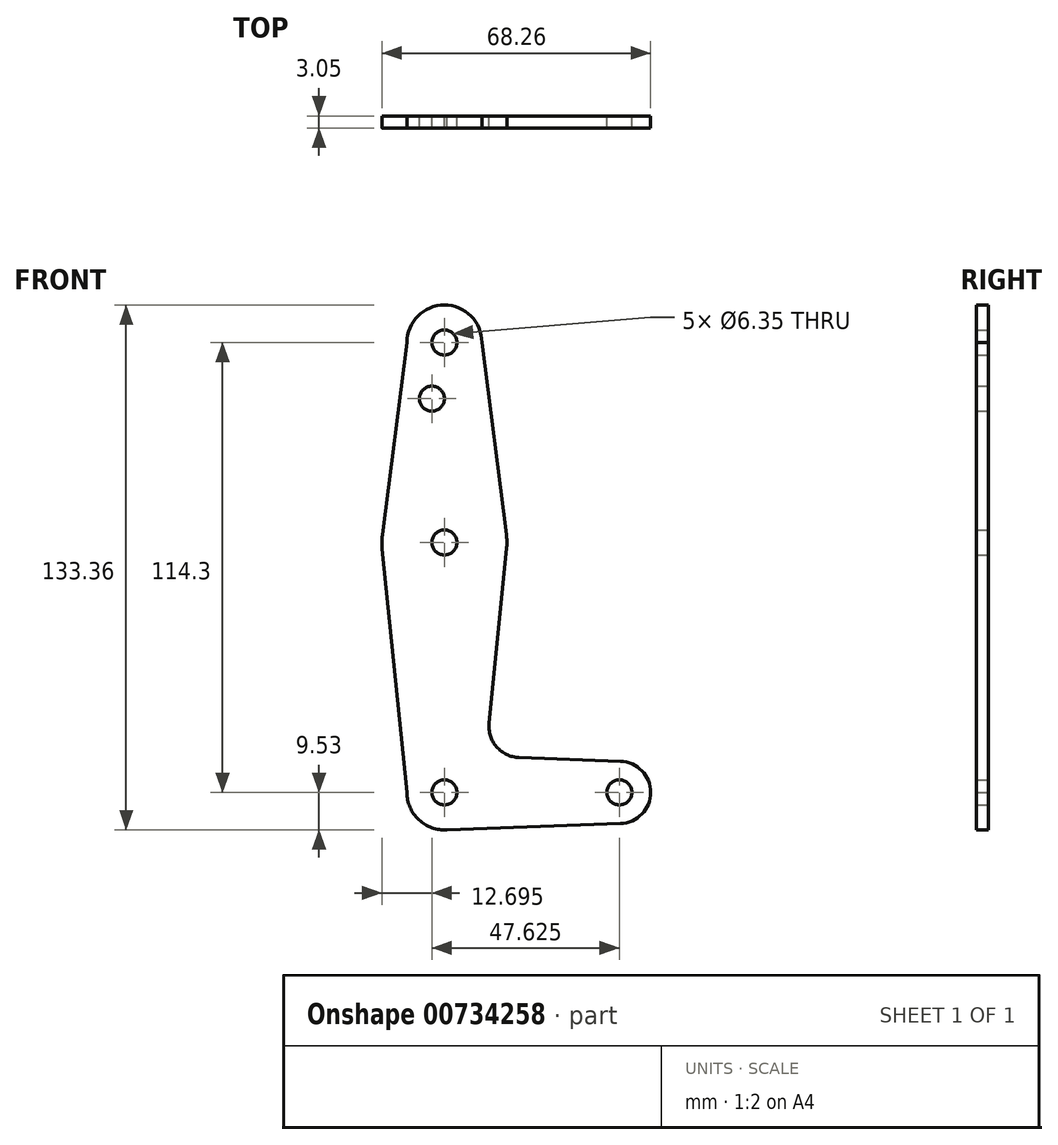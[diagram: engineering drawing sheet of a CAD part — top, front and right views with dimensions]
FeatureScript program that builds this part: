
annotation { "Feature Type Name" : "Feature", "Feature Type Description" : "" }
export const myFeature = defineFeature(function(context is Context, id is Id, definition is map)
    precondition{}
    {
        {
            var Q0;
            Q0=qCreatedBy(makeId("Front.planeOp"),FACE);
            var sketch = newSketch(context, id + "F0", { "sketchPlane" : qUnion([Q0])});
            skLineSegment(sketch, "E0", {"start": v(0, 0) * mm, "end": v(0, 114.3) * mm});
            skLineSegment(sketch, "E1", {"start": v(0, 0) * mm, "end": v(44.45, 0) * mm});
            skCircle(sketch, "E2", {"center": v(0, 114.3) * mm, "radius": 9.53 * mm});
            skCircle(sketch, "E3", {"center": v(0, 63.5) * mm, "radius": 15.88 * mm});
            skCircle(sketch, "E4", {"center": v(0, 0) * mm, "radius": 9.53 * mm});
            skCircle(sketch, "E5", {"center": v(44.45, 0) * mm, "radius": 7.94 * mm});
            skLineSegment(sketch, "E6", {"start": v(9.53, 114.3) * mm, "end": v(15.75, 65.5) * mm});
            skLineSegment(sketch, "E7", {"start": v(11.34, 17.6) * mm, "end": v(15.8, 61.91) * mm});
            skLineSegment(sketch, "E8", {"start": v(-9.53, 0) * mm, "end": v(-15.8, 61.9) * mm});
            skLineSegment(sketch, "E9", {"start": v(18.97, 8.85) * mm, "end": v(44.73, 7.93) * mm});
            skLineSegment(sketch, "E10", {"start": v(0, -9.53) * mm, "end": v(44.73, -7.93) * mm});
            skLineSegment(sketch, "E11", {"start": v(-9.53, 114.3) * mm, "end": v(-15.75, 65.5) * mm});
            skCircle(sketch, "E12", {"center": v(0, 114.3) * mm, "radius": 3.18 * mm});
            skCircle(sketch, "E13", {"center": v(-3.18, 100.03) * mm, "radius": 3.18 * mm});
            skCircle(sketch, "E14", {"center": v(0, 63.5) * mm, "radius": 3.18 * mm});
            skCircle(sketch, "E15", {"center": v(0, 0) * mm, "radius": 3.18 * mm});
            skCircle(sketch, "E16", {"center": v(44.45, 0) * mm, "radius": 3.18 * mm});
            skArc(sketch, "E17.filletArc", {"start": v(11.34, 17.6) * mm, "mid": v(13.26, 11.57) * mm, "end": v(18.97, 8.85) * mm});
            skSolve(sketch);
        }
        {
            var Q0;
            Q0 = qSketchRegion(id + "F0", true);
            var Q1;
            {var subQ0=sQuery(id+"F0.wireOp",EDGE,"E15");var subQ1=sQuery(id+"F0.wireOp",EDGE,"E0");var subQ2=makeQuery(id+"F0.imprint","INTERSECT",VERTEX,{"derivedFrom":[subQ1,subQ0]});Q1=makeQuery(id+"F0.imprint","IMPRINT",FACE,{"disambiguationData":[TD([[makeQuery(id+"F0.imprint","IMPRINT",EDGE,{"disambiguationData":[TD([[subQ2,-1.0]])],"derivedFrom":subQ1}),-1.0]])]});}
            extrude(context, id + "F1", {"entities" : qUnion([Q0, Q1]), "depth" : 3.05 * mm, "offsetDistance" : 25.4 * mm});
        }
    });
